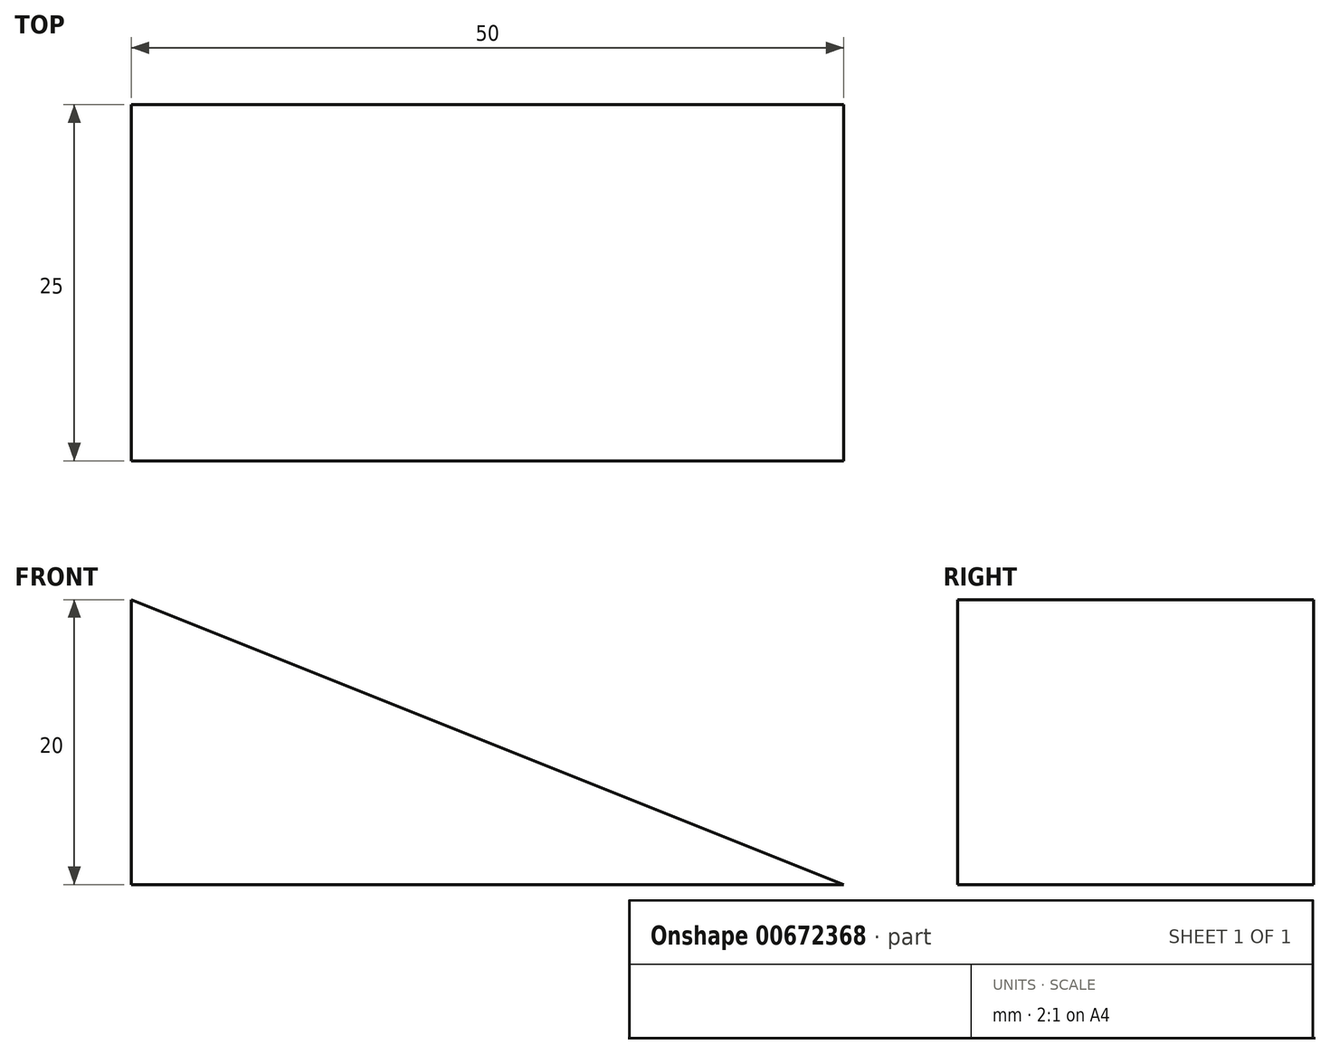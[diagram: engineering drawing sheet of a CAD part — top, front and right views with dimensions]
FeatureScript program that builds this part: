
annotation { "Feature Type Name" : "Feature", "Feature Type Description" : "" }
export const myFeature = defineFeature(function(context is Context, id is Id, definition is map)
    precondition{}
    {
        {
            var Q0;
            Q0=qCreatedBy(makeId("Front.planeOp"),FACE);
            var sketch = newSketch(context, id + "F0", { "sketchPlane" : qUnion([Q0])});
            skLineSegment(sketch, "E0", {"start": v(0, 0) * mm, "end": v(-50, 0) * mm});
            skLineSegment(sketch, "E1", {"start": v(-50, 0) * mm, "end": v(-50, 20) * mm});
            skLineSegment(sketch, "E2", {"start": v(-50, 20) * mm, "end": v(0, 0) * mm});
            skSolve(sketch);
        }
        {
            var Q0;
            Q0 = qSketchRegion(id + "F0", true);
            extrude(context, id + "F1", {"entities" : qUnion([Q0]), "depth" : 25 * mm, "offsetDistance" : 25 * mm});
        }
    });
